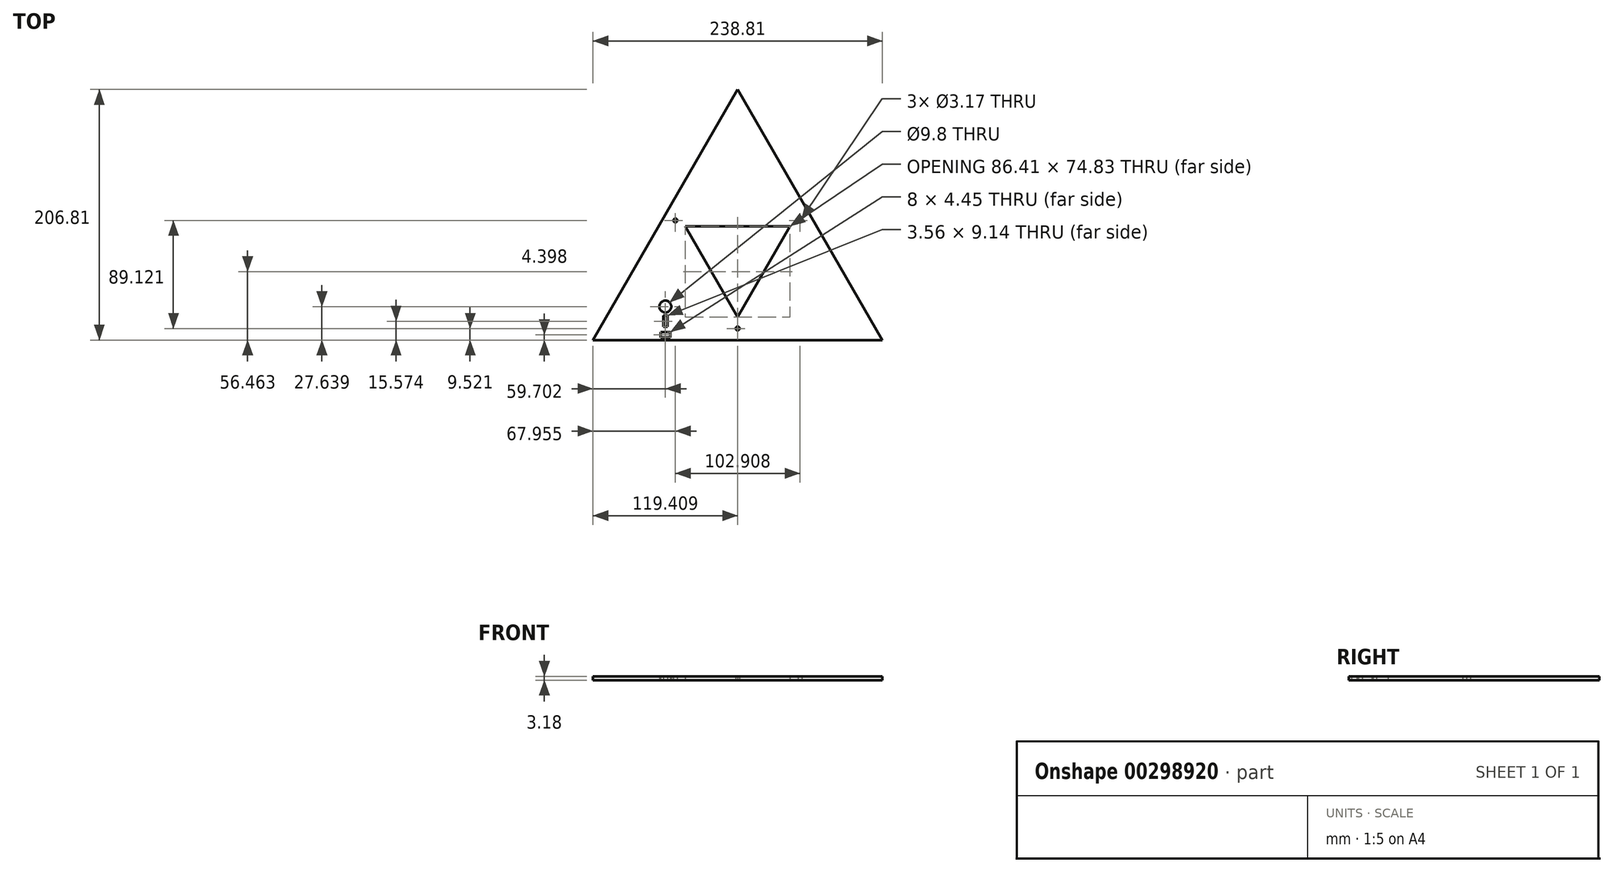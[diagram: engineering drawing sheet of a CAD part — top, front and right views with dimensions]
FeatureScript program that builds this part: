
annotation { "Feature Type Name" : "Feature", "Feature Type Description" : "" }
export const myFeature = defineFeature(function(context is Context, id is Id, definition is map)
    precondition{}
    {
        {
            var Q0;
            Q0=qCreatedBy(makeId("Top.planeOp"),FACE);
            var sketch = newSketch(context, id + "F0", { "sketchPlane" : qUnion([Q0])});
            skLineSegment(sketch, "E0", {"start": v(-43.2, 26.05) * mm, "end": v(0, -48.78) * mm});
            skLineSegment(sketch, "E1", {"start": v(43.21, 26.05) * mm, "end": v(0, -48.78) * mm});
            skLineSegment(sketch, "E2", {"start": v(119.41, -67.83) * mm, "end": v(-119.4, -67.83) * mm});
            skLineSegment(sketch, "E3", {"start": v(-119.4, -67.83) * mm, "end": v(0, 138.98) * mm});
            skLineSegment(sketch, "E4", {"start": v(0, 138.98) * mm, "end": v(119.41, -67.83) * mm});
            skLineSegment(sketch, "E5", {"start": v(43.21, 26.05) * mm, "end": v(-43.2, 26.05) * mm});
            skLineSegment(sketch, "E6", {"start": v(43.21, 26.05) * mm, "end": v(59.71, 35.57) * mm});
            skLineSegment(sketch, "E7", {"start": v(-43.2, 26.05) * mm, "end": v(-59.7, 35.57) * mm});
            skLineSegment(sketch, "E8", {"start": v(0, -48.78) * mm, "end": v(0, -67.83) * mm});
            skCircle(sketch, "E9", {"center": v(51.46, 30.81) * mm, "radius": 1.59 * mm});
            skCircle(sketch, "E10", {"center": v(-51.45, 30.81) * mm, "radius": 1.59 * mm});
            skCircle(sketch, "E11", {"center": v(0, -58.3) * mm, "radius": 1.59 * mm});
            skLineSegment(sketch, "E12", {"start": v(-59.7, -30.39) * mm, "end": v(-59.7, -40.2) * mm, "construction": true});
            skCircle(sketch, "E13", {"center": v(-59.7, -40.2) * mm, "radius": 4.9 * mm});
            skLineSegment(sketch, "E14", {"start": v(-59.7, -40.2) * mm, "end": v(-59.7, -52.26) * mm, "construction": true});
            skLineSegment(sketch, "E15", {"start": v(-59.7, -52.26) * mm, "end": v(-57.92, -52.26) * mm, "construction": true});
            skLineSegment(sketch, "E16", {"start": v(-59.7, -52.26) * mm, "end": v(-61.48, -52.26) * mm, "construction": true});
            skLineSegment(sketch, "E17", {"start": v(-61.48, -52.26) * mm, "end": v(-61.48, -47.68) * mm});
            skLineSegment(sketch, "E18", {"start": v(-57.92, -52.26) * mm, "end": v(-57.92, -47.68) * mm});
            skLineSegment(sketch, "E19", {"start": v(-61.48, -47.68) * mm, "end": v(-57.92, -47.68) * mm});
            skLineSegment(sketch, "E20", {"start": v(-61.48, -52.26) * mm, "end": v(-61.48, -56.83) * mm});
            skLineSegment(sketch, "E21", {"start": v(-57.92, -52.26) * mm, "end": v(-57.92, -56.83) * mm});
            skLineSegment(sketch, "E22", {"start": v(-61.48, -56.83) * mm, "end": v(-57.92, -56.83) * mm});
            skLineSegment(sketch, "E23", {"start": v(-59.7, -52.26) * mm, "end": v(-59.7, -63.43) * mm, "construction": true});
            skLineSegment(sketch, "E24", {"start": v(43.21, 26.05) * mm, "end": v(-21.6, -11.37) * mm, "construction": true});
            skLineSegment(sketch, "E25", {"start": v(0, -48.78) * mm, "end": v(0, 26.05) * mm, "construction": true});
            skLineSegment(sketch, "E26", {"start": v(-43.2, 26.05) * mm, "end": v(21.61, -11.37) * mm, "construction": true});
            skLineSegment(sketch, "E27", {"start": v(-21.6, -11.37) * mm, "end": v(-119.4, -67.83) * mm, "construction": true});
            skLineSegment(sketch, "E28", {"start": v(-59.7, -63.43) * mm, "end": v(-55.7, -63.43) * mm, "construction": true});
            skLineSegment(sketch, "E29", {"start": v(-59.7, -63.43) * mm, "end": v(-63.7, -63.43) * mm, "construction": true});
            skLineSegment(sketch, "E30", {"start": v(-63.7, -63.43) * mm, "end": v(-63.7, -61.2) * mm});
            skLineSegment(sketch, "E31", {"start": v(-55.7, -63.43) * mm, "end": v(-55.7, -61.2) * mm});
            skLineSegment(sketch, "E32", {"start": v(-55.7, -61.2) * mm, "end": v(-63.7, -61.2) * mm});
            skLineSegment(sketch, "E33", {"start": v(-63.7, -63.43) * mm, "end": v(-63.7, -65.66) * mm});
            skLineSegment(sketch, "E34", {"start": v(-55.7, -63.43) * mm, "end": v(-55.7, -65.66) * mm});
            skLineSegment(sketch, "E35", {"start": v(-55.7, -65.66) * mm, "end": v(-63.7, -65.66) * mm});
            skSolve(sketch);
        }
        {
            var Q0;
            {var subQ1=sQuery(id+"F0.wireOp",EDGE,"E1");Q0=makeQuery(id+"F0.imprint","IMPRINT",FACE,{"disambiguationData":[TD([[makeQuery(id+"F0.imprint","IMPRINT",EDGE,{"derivedFrom":subQ1}),1.0]])]});}
            var Q1;
            {var subQ1=sQuery(id+"F0.wireOp",EDGE,"E5");Q1=makeQuery(id+"F0.imprint","IMPRINT",FACE,{"disambiguationData":[TD([[makeQuery(id+"F0.imprint","IMPRINT",EDGE,{"derivedFrom":subQ1}),-1.0]])]});}
            var Q2;
            {var subQ6=sQuery(id+"F0.wireOp",EDGE,"E0");Q2=makeQuery(id+"F0.imprint","IMPRINT",FACE,{"disambiguationData":[TD([[makeQuery(id+"F0.imprint","IMPRINT",EDGE,{"derivedFrom":subQ6}),-1.0]])]});}
            extrude(context, id + "F1", {"entities" : qUnion([Q0, Q1, Q2]), "depth" : 3.17 * mm, "offsetDistance" : 25.4 * mm});
        }
    });
